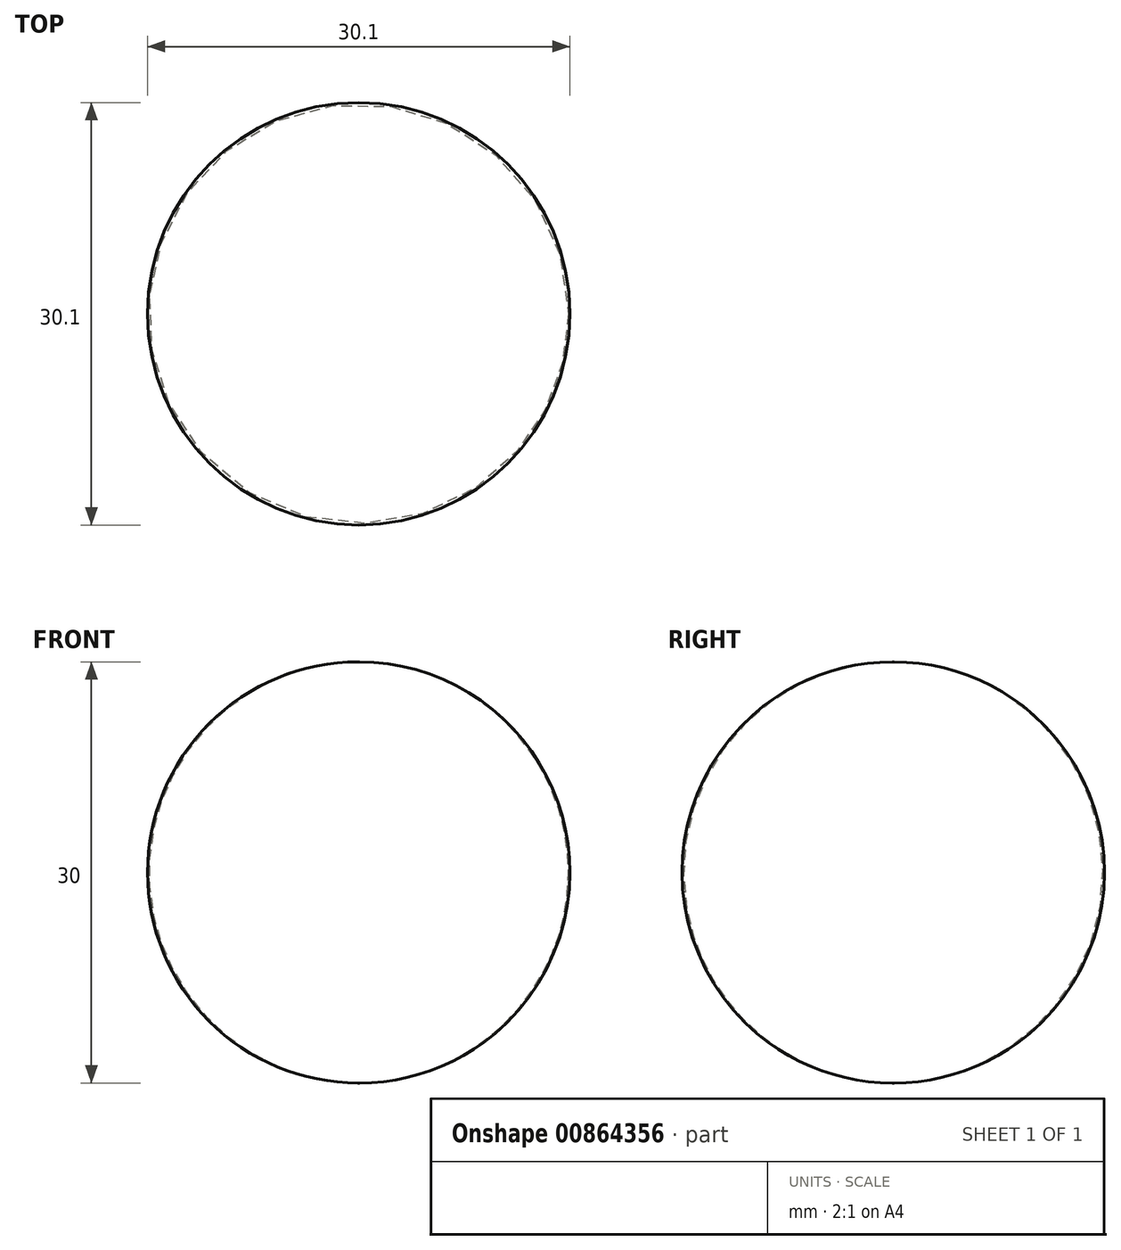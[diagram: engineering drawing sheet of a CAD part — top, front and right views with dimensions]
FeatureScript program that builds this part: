
annotation { "Feature Type Name" : "Feature", "Feature Type Description" : "" }
export const myFeature = defineFeature(function(context is Context, id is Id, definition is map)
    precondition{}
    {
        {
            var Q0;
            Q0=qCreatedBy(makeId("Front.planeOp"),FACE);
            var sketch = newSketch(context, id + "F0", { "sketchPlane" : qUnion([Q0])});
            skLineSegment(sketch, "E0", {"start": v(0, 0) * mm, "end": v(0, 30) * mm});
            skArc(sketch, "E1", {"start": v(0, 0) * mm, "mid": v(15.05, 15) * mm, "end": v(0, 30) * mm});
            skLineSegment(sketch, "E2", {"start": v(14.85, 17.44) * mm, "end": v(12.31, 17.44) * mm});
            skLineSegment(sketch, "E3", {"start": v(12.31, 17.44) * mm, "end": v(12.31, 14.44) * mm});
            skLineSegment(sketch, "E4", {"start": v(12.31, 14.44) * mm, "end": v(15.04, 14.44) * mm});
            skSolve(sketch);
        }
        {
            var Q0;
            {var subQ0=sQuery(id+"F0.wireOp",EDGE,"E2");Q0=makeQuery(id+"F0.imprint","IMPRINT",FACE,{"disambiguationData":[TD([[makeQuery(id+"F0.imprint","IMPRINT",EDGE,{"derivedFrom":subQ0}),1.0]])]});}
            var Q1;
            {var subQ2=sQuery(id+"F0.wireOp",EDGE,"E0");Q1=makeQuery(id+"F0.imprint","IMPRINT",FACE,{"disambiguationData":[TD([[makeQuery(id+"F0.imprint","IMPRINT",EDGE,{"derivedFrom":subQ2}),-1.0]])]});}
            var Q2;
            Q2=sQuery(id+"F0.wireOp",EDGE,"E0");
            revolve(context, id + "F1", {"surfaceOperationType" : NewSurfaceOperationType.NEW, "entities" : qUnion([Q0, Q1]), "axis" : qUnion([Q2]), "revolveType" : RevolveType.FULL});
        }
    });
